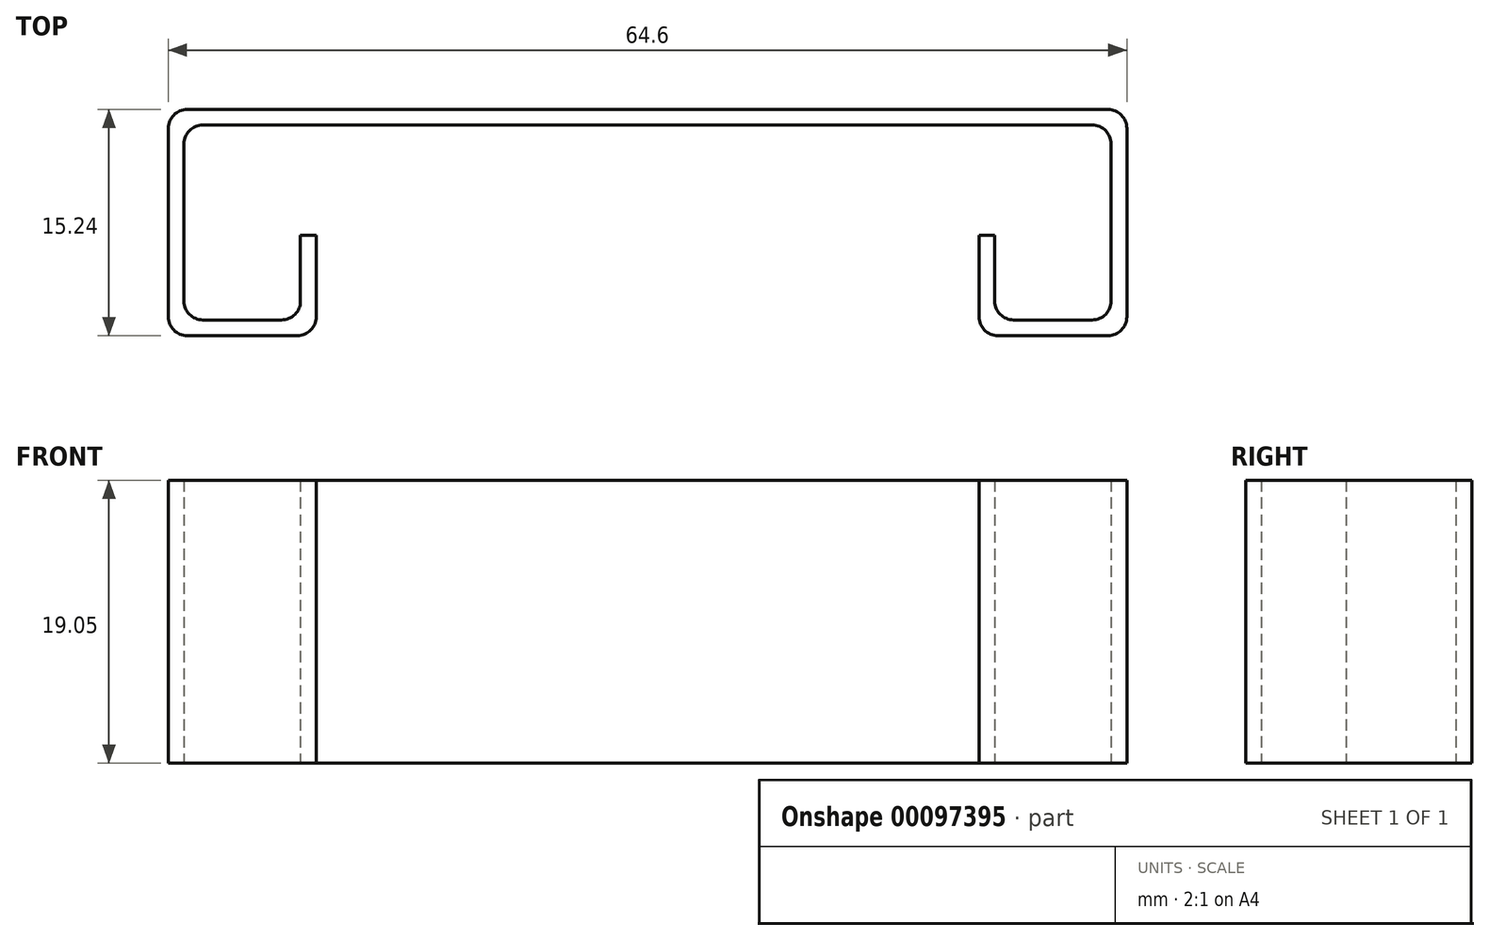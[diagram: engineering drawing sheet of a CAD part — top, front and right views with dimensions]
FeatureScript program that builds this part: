
annotation { "Feature Type Name" : "Feature", "Feature Type Description" : "" }
export const myFeature = defineFeature(function(context is Context, id is Id, definition is map)
    precondition{}
    {
        {
            var Q0;
            Q0=qCreatedBy(makeId("Top.planeOp"),FACE);
            var sketch = newSketch(context, id + "F0", { "sketchPlane" : qUnion([Q0])});
            skLineSegment(sketch, "E0", {"start": v(1.27, 0) * mm, "end": v(8.7, 0) * mm});
            skLineSegment(sketch, "E1", {"start": v(9.96, 1.27) * mm, "end": v(9.96, 6.77) * mm});
            skLineSegment(sketch, "E2", {"start": v(9.96, 6.77) * mm, "end": v(8.9, 6.77) * mm});
            skLineSegment(sketch, "E3", {"start": v(8.9, 6.77) * mm, "end": v(8.9, 2.33) * mm});
            skLineSegment(sketch, "E4", {"start": v(7.64, 1.06) * mm, "end": v(2.33, 1.06) * mm});
            skLineSegment(sketch, "E5", {"start": v(1.06, 2.33) * mm, "end": v(1.06, 12.91) * mm});
            skLineSegment(sketch, "E6", {"start": v(2.33, 14.18) * mm, "end": v(32.3, 14.18) * mm});
            skLineSegment(sketch, "E7", {"start": v(32.3, 14.18) * mm, "end": v(32.3, 15.24) * mm});
            skLineSegment(sketch, "E8", {"start": v(32.3, 15.24) * mm, "end": v(1.27, 15.24) * mm});
            skLineSegment(sketch, "E9", {"start": v(0, 13.97) * mm, "end": v(0, 1.27) * mm});
            skPoint(sketch, "E10.visualSharp", {"position": v(8.9, 1.06) * mm});
            skArc(sketch, "E10.filletArc", {"start": v(7.64, 1.06) * mm, "mid": v(8.53, 1.43) * mm, "end": v(8.9, 2.33) * mm});
            skPoint(sketch, "E11.visualSharp", {"position": v(1.06, 1.06) * mm});
            skArc(sketch, "E11.filletArc", {"start": v(1.06, 2.33) * mm, "mid": v(1.43, 1.43) * mm, "end": v(2.33, 1.06) * mm});
            skPoint(sketch, "E12.visualSharp", {"position": v(0, 0) * mm});
            skArc(sketch, "E12.filletArc", {"start": v(0, 1.27) * mm, "mid": v(0.37, 0.37) * mm, "end": v(1.27, 0) * mm});
            skPoint(sketch, "E13.visualSharp", {"position": v(9.96, 0) * mm});
            skArc(sketch, "E13.filletArc", {"start": v(8.7, 0) * mm, "mid": v(9.6, 0.37) * mm, "end": v(9.96, 1.27) * mm});
            skPoint(sketch, "E14.visualSharp", {"position": v(0, 15.24) * mm});
            skArc(sketch, "E14.filletArc", {"start": v(1.27, 15.24) * mm, "mid": v(0.37, 14.87) * mm, "end": v(0, 13.97) * mm});
            skPoint(sketch, "E15.visualSharp", {"position": v(1.06, 14.18) * mm});
            skArc(sketch, "E15.filletArc", {"start": v(2.33, 14.18) * mm, "mid": v(1.43, 13.8) * mm, "end": v(1.06, 12.91) * mm});
            skSolve(sketch);
        }
        {
            var Q0;
            Q0=makeQuery(id+"F0.imprint","IMPRINT",FACE,{"disambiguationData":[TD([[makeQuery(id+"F0.imprint","IMPRINT",EDGE,{"derivedFrom":sQuery(id+"F0.wireOp",EDGE,"E0")}),1.0]])]});
            extrude(context, id + "F1", {"entities" : qUnion([Q0]), "depth" : 19.05 * mm});
        }
        {
            var Q0;
            Q0=makeQuery(id+"F1.opExtrude","SWEPT_BODY",BODY,{"disambiguationData":[OSD([sQuery(id+"F0.wireOp",EDGE,"E0"),sQuery(id+"F0.wireOp",EDGE,"E1"),sQuery(id+"F0.wireOp",EDGE,"E2"),sQuery(id+"F0.wireOp",EDGE,"E3"),sQuery(id+"F0.wireOp",EDGE,"E4"),sQuery(id+"F0.wireOp",EDGE,"E5"),sQuery(id+"F0.wireOp",EDGE,"E6"),sQuery(id+"F0.wireOp",EDGE,"E7"),sQuery(id+"F0.wireOp",EDGE,"E8"),sQuery(id+"F0.wireOp",EDGE,"E9"),sQuery(id+"F0.wireOp",EDGE,"E10.filletArc"),sQuery(id+"F0.wireOp",EDGE,"E11.filletArc"),sQuery(id+"F0.wireOp",EDGE,"E12.filletArc"),sQuery(id+"F0.wireOp",EDGE,"E13.filletArc"),sQuery(id+"F0.wireOp",EDGE,"E14.filletArc"),sQuery(id+"F0.wireOp",EDGE,"E15.filletArc")])]});
            var Q1;
            Q1=makeQuery(id+"F1.opExtrude","SWEPT_FACE",FACE,{"disambiguationData":[OSD([sQuery(id+"F0.wireOp",EDGE,"E7")])]});
            mirror(context, id + "F2", {"operationType" : NewBodyOperationType.ADD, "entities" : qUnion([Q0]), "mirrorPlane" : qUnion([Q1])});
        }
    });
